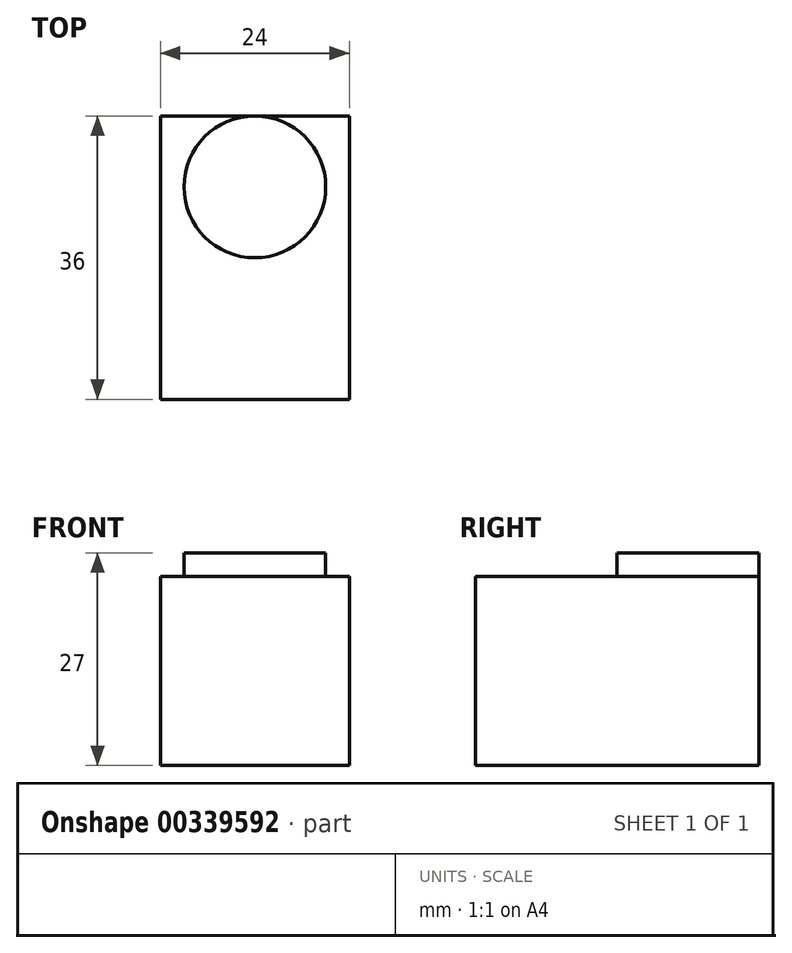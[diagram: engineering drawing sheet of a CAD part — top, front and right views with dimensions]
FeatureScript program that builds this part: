
annotation { "Feature Type Name" : "Feature", "Feature Type Description" : "" }
export const myFeature = defineFeature(function(context is Context, id is Id, definition is map)
    precondition{}
    {
        {
            var Q0;
            Q0=qCreatedBy(makeId("Top.planeOp"),FACE);
            var sketch = newSketch(context, id + "F0", { "sketchPlane" : qUnion([Q0])});
            skLineSegment(sketch, "E0.bottom", {"start": v(-10.7, 22.88) * mm, "end": v(13.3, 22.88) * mm});
            skLineSegment(sketch, "E0.top", {"start": v(-10.7, -13.12) * mm, "end": v(13.3, -13.12) * mm});
            skLineSegment(sketch, "E0.left", {"start": v(-10.7, 22.88) * mm, "end": v(-10.7, -13.12) * mm});
            skLineSegment(sketch, "E0.right", {"start": v(13.3, 22.88) * mm, "end": v(13.3, -13.12) * mm});
            skCircle(sketch, "E1", {"center": v(1.3, 13.88) * mm, "radius": 9 * mm});
            skSolve(sketch);
        }
        {
            var Q0;
            Q0=makeQuery(id+"F0.imprint","IMPRINT",FACE,{"disambiguationData":[TD([[makeQuery(id+"F0.imprint","IMPRINT",EDGE,{"derivedFrom":sQuery(id+"F0.wireOp",EDGE,"E0.top")}),1.0]])]});
            var Q1;
            Q1=makeQuery(id+"F0.imprint","IMPRINT",FACE,{"disambiguationData":[TD([[makeQuery(id+"F0.imprint","IMPRINT",EDGE,{"derivedFrom":sQuery(id+"F0.wireOp",EDGE,"E1")}),1.0]])]});
            extrude(context, id + "F1", {"entities" : qUnion([Q0, Q1]), "depth" : -24 * mm});
        }
        {
            var Q0;
            Q0=makeQuery(id+"F0.imprint","IMPRINT",FACE,{"disambiguationData":[TD([[makeQuery(id+"F0.imprint","IMPRINT",EDGE,{"derivedFrom":sQuery(id+"F0.wireOp",EDGE,"E1")}),1.0]])]});
            extrude(context, id + "F2", {"entities" : qUnion([Q0]), "depth" : 3 * mm});
        }
    });
